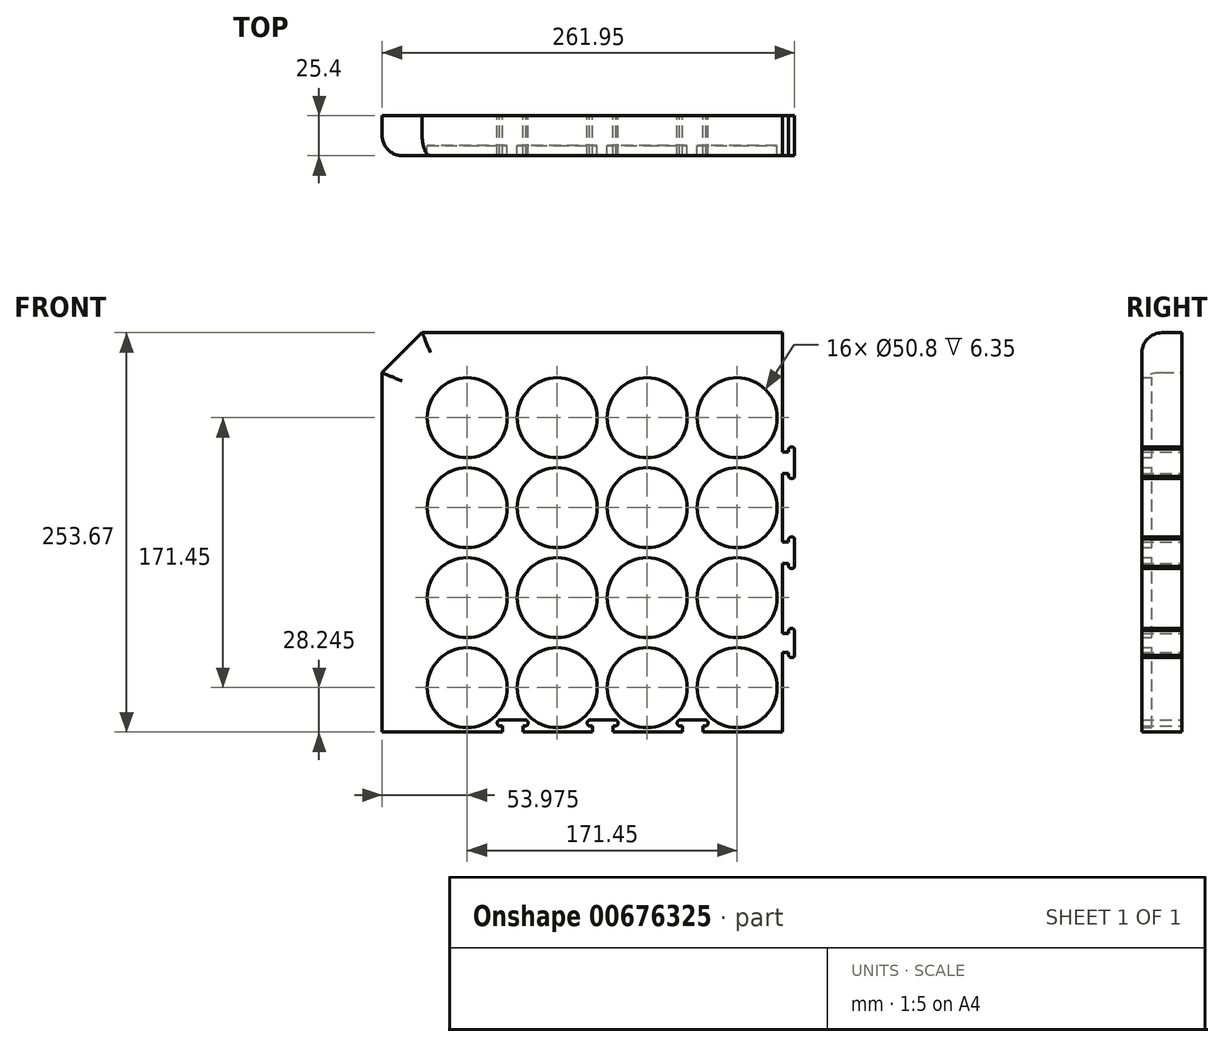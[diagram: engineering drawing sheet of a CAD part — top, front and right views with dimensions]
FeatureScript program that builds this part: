
annotation { "Feature Type Name" : "Feature", "Feature Type Description" : "" }
export const myFeature = defineFeature(function(context is Context, id is Id, definition is map)
    precondition{}
    {
        {
            var Q0;
            Q0=qCreatedBy(makeId("Front.planeOp"),FACE);
            var sketch = newSketch(context, id + "F0", { "sketchPlane" : qUnion([Q0])});
            skLineSegment(sketch, "E0", {"start": v(0, 0) * mm, "end": v(457.2, 0) * mm});
            skLineSegment(sketch, "E1", {"start": v(457.2, 0) * mm, "end": v(457.2, 457.2) * mm});
            skLineSegment(sketch, "E2", {"start": v(0, 0) * mm, "end": v(0, 457.2) * mm});
            skLineSegment(sketch, "E3", {"start": v(0, 457.2) * mm, "end": v(457.2, 457.2) * mm});
            skLineSegment(sketch, "E4", {"start": v(0, 457.2) * mm, "end": v(57.15, 457.2) * mm, "construction": true});
            skLineSegment(sketch, "E5", {"start": v(0, 457.2) * mm, "end": v(0, 400.05) * mm});
            skLineSegment(sketch, "E6", {"start": v(0, 400.05) * mm, "end": v(57.15, 400.05) * mm, "construction": true});
            skLineSegment(sketch, "E7", {"start": v(57.15, 457.2) * mm, "end": v(57.15, 400.05) * mm, "construction": true});
            skLineSegment(sketch, "E8", {"start": v(0, 457.2) * mm, "end": v(57.15, 400.05) * mm, "construction": true});
            skPoint(sketch, "E9.first.point", {"position": v(0, 428.63) * mm});
            skPoint(sketch, "E9.second.point", {"position": v(57.15, 428.63) * mm});
            skPoint(sketch, "E9.third.point", {"position": v(28.58, 457.2) * mm});
            skCircle(sketch, "E10", {"center": v(28.58, 428.63) * mm, "radius": 25.4 * mm});
            skCircle(sketch, "E11.0.1.0", {"center": v(28.58, 371.48) * mm, "radius": 25.4 * mm});
            skCircle(sketch, "E11.0.2.0", {"center": v(28.58, 314.32) * mm, "radius": 25.4 * mm});
            skCircle(sketch, "E11.0.3.0", {"center": v(28.58, 257.17) * mm, "radius": 25.4 * mm});
            skCircle(sketch, "E11.0.4.0", {"center": v(28.58, 200.02) * mm, "radius": 25.4 * mm});
            skCircle(sketch, "E11.0.5.0", {"center": v(28.58, 142.87) * mm, "radius": 25.4 * mm});
            skCircle(sketch, "E11.0.6.0", {"center": v(28.58, 85.72) * mm, "radius": 25.4 * mm});
            skCircle(sketch, "E11.0.7.0", {"center": v(28.58, 28.57) * mm, "radius": 25.4 * mm});
            skCircle(sketch, "E11.1.0.0", {"center": v(85.73, 428.63) * mm, "radius": 25.4 * mm});
            skCircle(sketch, "E11.1.1.0", {"center": v(85.73, 371.48) * mm, "radius": 25.4 * mm});
            skCircle(sketch, "E11.1.2.0", {"center": v(85.73, 314.32) * mm, "radius": 25.4 * mm});
            skCircle(sketch, "E11.1.3.0", {"center": v(85.73, 257.17) * mm, "radius": 25.4 * mm});
            skCircle(sketch, "E11.1.4.0", {"center": v(85.73, 200.02) * mm, "radius": 25.4 * mm});
            skCircle(sketch, "E11.1.5.0", {"center": v(85.73, 142.87) * mm, "radius": 25.4 * mm});
            skCircle(sketch, "E11.1.6.0", {"center": v(85.73, 85.72) * mm, "radius": 25.4 * mm});
            skCircle(sketch, "E11.1.7.0", {"center": v(85.73, 28.57) * mm, "radius": 25.4 * mm});
            skCircle(sketch, "E11.2.0.0", {"center": v(142.88, 428.63) * mm, "radius": 25.4 * mm});
            skCircle(sketch, "E11.2.1.0", {"center": v(142.88, 371.48) * mm, "radius": 25.4 * mm});
            skCircle(sketch, "E11.2.2.0", {"center": v(142.88, 314.32) * mm, "radius": 25.4 * mm});
            skCircle(sketch, "E11.2.3.0", {"center": v(142.88, 257.17) * mm, "radius": 25.4 * mm});
            skCircle(sketch, "E11.2.4.0", {"center": v(142.88, 200.02) * mm, "radius": 25.4 * mm});
            skCircle(sketch, "E11.2.5.0", {"center": v(142.88, 142.87) * mm, "radius": 25.4 * mm});
            skCircle(sketch, "E11.2.6.0", {"center": v(142.88, 85.72) * mm, "radius": 25.4 * mm});
            skCircle(sketch, "E11.2.7.0", {"center": v(142.88, 28.57) * mm, "radius": 25.4 * mm});
            skCircle(sketch, "E11.3.0.0", {"center": v(200.03, 428.63) * mm, "radius": 25.4 * mm});
            skCircle(sketch, "E11.3.1.0", {"center": v(200.03, 371.48) * mm, "radius": 25.4 * mm});
            skCircle(sketch, "E11.3.2.0", {"center": v(200.03, 314.32) * mm, "radius": 25.4 * mm});
            skCircle(sketch, "E11.3.3.0", {"center": v(200.03, 257.17) * mm, "radius": 25.4 * mm});
            skCircle(sketch, "E11.3.4.0", {"center": v(200.03, 200.02) * mm, "radius": 25.4 * mm});
            skCircle(sketch, "E11.3.5.0", {"center": v(200.03, 142.87) * mm, "radius": 25.4 * mm});
            skCircle(sketch, "E11.3.6.0", {"center": v(200.03, 85.72) * mm, "radius": 25.4 * mm});
            skCircle(sketch, "E11.3.7.0", {"center": v(200.03, 28.57) * mm, "radius": 25.4 * mm});
            skCircle(sketch, "E11.4.0.0", {"center": v(257.18, 428.63) * mm, "radius": 25.4 * mm});
            skCircle(sketch, "E11.4.1.0", {"center": v(257.18, 371.48) * mm, "radius": 25.4 * mm});
            skCircle(sketch, "E11.4.2.0", {"center": v(257.18, 314.32) * mm, "radius": 25.4 * mm});
            skCircle(sketch, "E11.4.3.0", {"center": v(257.18, 257.17) * mm, "radius": 25.4 * mm});
            skCircle(sketch, "E11.4.4.0", {"center": v(257.18, 200.02) * mm, "radius": 25.4 * mm});
            skCircle(sketch, "E11.4.5.0", {"center": v(257.18, 142.87) * mm, "radius": 25.4 * mm});
            skCircle(sketch, "E11.4.6.0", {"center": v(257.18, 85.72) * mm, "radius": 25.4 * mm});
            skCircle(sketch, "E11.4.7.0", {"center": v(257.18, 28.57) * mm, "radius": 25.4 * mm});
            skCircle(sketch, "E11.5.0.0", {"center": v(314.33, 428.63) * mm, "radius": 25.4 * mm});
            skCircle(sketch, "E11.5.1.0", {"center": v(314.33, 371.48) * mm, "radius": 25.4 * mm});
            skCircle(sketch, "E11.5.2.0", {"center": v(314.33, 314.32) * mm, "radius": 25.4 * mm});
            skCircle(sketch, "E11.5.3.0", {"center": v(314.33, 257.17) * mm, "radius": 25.4 * mm});
            skCircle(sketch, "E11.5.4.0", {"center": v(314.33, 200.02) * mm, "radius": 25.4 * mm});
            skCircle(sketch, "E11.5.5.0", {"center": v(314.33, 142.87) * mm, "radius": 25.4 * mm});
            skCircle(sketch, "E11.5.6.0", {"center": v(314.33, 85.72) * mm, "radius": 25.4 * mm});
            skCircle(sketch, "E11.5.7.0", {"center": v(314.33, 28.57) * mm, "radius": 25.4 * mm});
            skCircle(sketch, "E11.6.0.0", {"center": v(371.48, 428.63) * mm, "radius": 25.4 * mm});
            skCircle(sketch, "E11.6.1.0", {"center": v(371.48, 371.48) * mm, "radius": 25.4 * mm});
            skCircle(sketch, "E11.6.2.0", {"center": v(371.48, 314.32) * mm, "radius": 25.4 * mm});
            skCircle(sketch, "E11.6.3.0", {"center": v(371.48, 257.17) * mm, "radius": 25.4 * mm});
            skCircle(sketch, "E11.6.4.0", {"center": v(371.48, 200.02) * mm, "radius": 25.4 * mm});
            skCircle(sketch, "E11.6.5.0", {"center": v(371.48, 142.87) * mm, "radius": 25.4 * mm});
            skCircle(sketch, "E11.6.6.0", {"center": v(371.48, 85.72) * mm, "radius": 25.4 * mm});
            skCircle(sketch, "E11.6.7.0", {"center": v(371.48, 28.57) * mm, "radius": 25.4 * mm});
            skCircle(sketch, "E11.7.0.0", {"center": v(428.63, 428.63) * mm, "radius": 25.4 * mm});
            skCircle(sketch, "E11.7.1.0", {"center": v(428.63, 371.48) * mm, "radius": 25.4 * mm});
            skCircle(sketch, "E11.7.2.0", {"center": v(428.63, 314.32) * mm, "radius": 25.4 * mm});
            skCircle(sketch, "E11.7.3.0", {"center": v(428.63, 257.17) * mm, "radius": 25.4 * mm});
            skCircle(sketch, "E11.7.4.0", {"center": v(428.63, 200.02) * mm, "radius": 25.4 * mm});
            skCircle(sketch, "E11.7.5.0", {"center": v(428.63, 142.87) * mm, "radius": 25.4 * mm});
            skCircle(sketch, "E11.7.6.0", {"center": v(428.63, 85.72) * mm, "radius": 25.4 * mm});
            skCircle(sketch, "E11.7.7.0", {"center": v(428.63, 28.57) * mm, "radius": 25.4 * mm});
            skLineSegment(sketch, "E11.direction1", {"start": v(28.58, 428.63) * mm, "end": v(85.73, 428.63) * mm, "construction": true});
            skLineSegment(sketch, "E11.direction2", {"start": v(28.58, 428.63) * mm, "end": v(28.58, 371.48) * mm, "construction": true});
            skLineSegment(sketch, "E12", {"start": v(0, 457.2) * mm, "end": v(0, 228.6) * mm, "construction": true});
            skLineSegment(sketch, "E13", {"start": v(0, 228.6) * mm, "end": v(-25.4, 228.6) * mm, "construction": true});
            skLineSegment(sketch, "E14", {"start": v(0, 0) * mm, "end": v(-25.4, 0) * mm, "construction": true});
            skLineSegment(sketch, "E15", {"start": v(0, 0) * mm, "end": v(0, -25.4) * mm, "construction": true});
            skLineSegment(sketch, "E16", {"start": v(457.2, 0) * mm, "end": v(458.14, -25.38) * mm, "construction": true});
            skLineSegment(sketch, "E17", {"start": v(457.2, 0) * mm, "end": v(482.58, 0.94) * mm, "construction": true});
            skLineSegment(sketch, "E18", {"start": v(457.2, 457.2) * mm, "end": v(457.2, 482.6) * mm, "construction": true});
            skLineSegment(sketch, "E19", {"start": v(457.2, 457.2) * mm, "end": v(482.6, 457.2) * mm, "construction": true});
            skLineSegment(sketch, "E20", {"start": v(0, 457.2) * mm, "end": v(0, 482.6) * mm, "construction": true});
            skLineSegment(sketch, "E21", {"start": v(0, 457.2) * mm, "end": v(-25.4, 457.2) * mm, "construction": true});
            skLineSegment(sketch, "E22", {"start": v(-25.4, 228.6) * mm, "end": v(-25.4, 0) * mm});
            skLineSegment(sketch, "E23", {"start": v(0, -25.4) * mm, "end": v(-25.4, 0) * mm});
            skLineSegment(sketch, "E24", {"start": v(0, -25.4) * mm, "end": v(458.14, -25.38) * mm});
            skLineSegment(sketch, "E25", {"start": v(458.14, -25.38) * mm, "end": v(482.58, 0.94) * mm});
            skLineSegment(sketch, "E26", {"start": v(482.58, 0.94) * mm, "end": v(482.6, 457.2) * mm});
            skLineSegment(sketch, "E27", {"start": v(482.6, 457.2) * mm, "end": v(457.2, 482.6) * mm});
            skLineSegment(sketch, "E28", {"start": v(457.2, 482.6) * mm, "end": v(0, 482.6) * mm});
            skLineSegment(sketch, "E29", {"start": v(0, 482.6) * mm, "end": v(-25.4, 457.2) * mm});
            skLineSegment(sketch, "E30", {"start": v(-25.4, 457.2) * mm, "end": v(-25.4, 228.6) * mm});
            skLineSegment(sketch, "E31", {"start": v(229.07, -25.4) * mm, "end": v(229.07, 482.6) * mm, "construction": true});
            skLineSegment(sketch, "E32", {"start": v(482.6, 228.6) * mm, "end": v(-25.4, 228.6) * mm, "construction": true});
            skPoint(sketch, "E32.startSnap0", {"position": v(457.2, 228.6) * mm});
            skSolve(sketch);
        }
        {
            var Q0;
            Q0=makeQuery(id+"F0.imprint","IMPRINT",FACE,{"disambiguationData":[TD([[makeQuery(id+"F0.imprint","IMPRINT",EDGE,{"derivedFrom":sQuery(id+"F0.wireOp",EDGE,"E0")}),1.0]])]});
            var Q1;
            Q1=makeQuery(id+"F0.imprint","IMPRINT",FACE,{"disambiguationData":[TD([[makeQuery(id+"F0.imprint","IMPRINT",EDGE,{"derivedFrom":sQuery(id+"F0.wireOp",EDGE,"E0")}),-1.0]])]});
            extrude(context, id + "F1", {"entities" : qUnion([Q0, Q1]), "depth" : 25.4 * mm, "offsetDistance" : 25.4 * mm});
        }
        {
            var Q0;
            Q0=makeQuery(id+"F0.imprint","IMPRINT",FACE,{"disambiguationData":[TD([[makeQuery(id+"F0.imprint","IMPRINT",EDGE,{"derivedFrom":sQuery(id+"F0.wireOp",EDGE,"E10")}),1.0]])]});
            var Q1;
            Q1=makeQuery(id+"F0.imprint","IMPRINT",FACE,{"disambiguationData":[TD([[makeQuery(id+"F0.imprint","IMPRINT",EDGE,{"derivedFrom":sQuery(id+"F0.wireOp",EDGE,"E11.1.0.0")}),1.0]])]});
            var Q2;
            Q2=makeQuery(id+"F0.imprint","IMPRINT",FACE,{"disambiguationData":[TD([[makeQuery(id+"F0.imprint","IMPRINT",EDGE,{"derivedFrom":sQuery(id+"F0.wireOp",EDGE,"E11.2.0.0")}),1.0]])]});
            var Q3;
            Q3=makeQuery(id+"F0.imprint","IMPRINT",FACE,{"disambiguationData":[TD([[makeQuery(id+"F0.imprint","IMPRINT",EDGE,{"derivedFrom":sQuery(id+"F0.wireOp",EDGE,"E11.3.0.0")}),1.0]])]});
            var Q4;
            Q4=makeQuery(id+"F0.imprint","IMPRINT",FACE,{"disambiguationData":[TD([[makeQuery(id+"F0.imprint","IMPRINT",EDGE,{"derivedFrom":sQuery(id+"F0.wireOp",EDGE,"E11.4.0.0")}),1.0]])]});
            var Q5;
            Q5=makeQuery(id+"F0.imprint","IMPRINT",FACE,{"disambiguationData":[TD([[makeQuery(id+"F0.imprint","IMPRINT",EDGE,{"derivedFrom":sQuery(id+"F0.wireOp",EDGE,"E11.5.0.0")}),1.0]])]});
            var Q6;
            Q6=makeQuery(id+"F0.imprint","IMPRINT",FACE,{"disambiguationData":[TD([[makeQuery(id+"F0.imprint","IMPRINT",EDGE,{"derivedFrom":sQuery(id+"F0.wireOp",EDGE,"E11.6.0.0")}),1.0]])]});
            var Q7;
            Q7=makeQuery(id+"F0.imprint","IMPRINT",FACE,{"disambiguationData":[TD([[makeQuery(id+"F0.imprint","IMPRINT",EDGE,{"derivedFrom":sQuery(id+"F0.wireOp",EDGE,"E11.7.0.0")}),1.0]])]});
            var Q8;
            Q8=makeQuery(id+"F0.imprint","IMPRINT",FACE,{"disambiguationData":[TD([[makeQuery(id+"F0.imprint","IMPRINT",EDGE,{"derivedFrom":sQuery(id+"F0.wireOp",EDGE,"E11.7.1.0")}),1.0]])]});
            var Q9;
            Q9=makeQuery(id+"F0.imprint","IMPRINT",FACE,{"disambiguationData":[TD([[makeQuery(id+"F0.imprint","IMPRINT",EDGE,{"derivedFrom":sQuery(id+"F0.wireOp",EDGE,"E11.6.1.0")}),1.0]])]});
            var Q10;
            Q10=makeQuery(id+"F0.imprint","IMPRINT",FACE,{"disambiguationData":[TD([[makeQuery(id+"F0.imprint","IMPRINT",EDGE,{"derivedFrom":sQuery(id+"F0.wireOp",EDGE,"E11.5.1.0")}),1.0]])]});
            var Q11;
            Q11=makeQuery(id+"F0.imprint","IMPRINT",FACE,{"disambiguationData":[TD([[makeQuery(id+"F0.imprint","IMPRINT",EDGE,{"derivedFrom":sQuery(id+"F0.wireOp",EDGE,"E11.4.1.0")}),1.0]])]});
            var Q12;
            Q12=makeQuery(id+"F0.imprint","IMPRINT",FACE,{"disambiguationData":[TD([[makeQuery(id+"F0.imprint","IMPRINT",EDGE,{"derivedFrom":sQuery(id+"F0.wireOp",EDGE,"E11.3.1.0")}),1.0]])]});
            var Q13;
            Q13=makeQuery(id+"F0.imprint","IMPRINT",FACE,{"disambiguationData":[TD([[makeQuery(id+"F0.imprint","IMPRINT",EDGE,{"derivedFrom":sQuery(id+"F0.wireOp",EDGE,"E11.2.3.0")}),1.0]])]});
            var Q14;
            Q14=makeQuery(id+"F0.imprint","IMPRINT",FACE,{"disambiguationData":[TD([[makeQuery(id+"F0.imprint","IMPRINT",EDGE,{"derivedFrom":sQuery(id+"F0.wireOp",EDGE,"E11.6.3.0")}),1.0]])]});
            var Q15;
            Q15=makeQuery(id+"F0.imprint","IMPRINT",FACE,{"disambiguationData":[TD([[makeQuery(id+"F0.imprint","IMPRINT",EDGE,{"derivedFrom":sQuery(id+"F0.wireOp",EDGE,"E11.4.3.0")}),1.0]])]});
            var Q16;
            Q16=makeQuery(id+"F0.imprint","IMPRINT",FACE,{"disambiguationData":[TD([[makeQuery(id+"F0.imprint","IMPRINT",EDGE,{"derivedFrom":sQuery(id+"F0.wireOp",EDGE,"E11.5.2.0")}),1.0]])]});
            var Q17;
            Q17=makeQuery(id+"F0.imprint","IMPRINT",FACE,{"disambiguationData":[TD([[makeQuery(id+"F0.imprint","IMPRINT",EDGE,{"derivedFrom":sQuery(id+"F0.wireOp",EDGE,"E11.3.2.0")}),1.0]])]});
            var Q18;
            Q18=makeQuery(id+"F0.imprint","IMPRINT",FACE,{"disambiguationData":[TD([[makeQuery(id+"F0.imprint","IMPRINT",EDGE,{"derivedFrom":sQuery(id+"F0.wireOp",EDGE,"E11.2.4.0")}),1.0]])]});
            var Q19;
            Q19=makeQuery(id+"F0.imprint","IMPRINT",FACE,{"disambiguationData":[TD([[makeQuery(id+"F0.imprint","IMPRINT",EDGE,{"derivedFrom":sQuery(id+"F0.wireOp",EDGE,"E11.6.4.0")}),1.0]])]});
            var Q20;
            Q20=makeQuery(id+"F0.imprint","IMPRINT",FACE,{"disambiguationData":[TD([[makeQuery(id+"F0.imprint","IMPRINT",EDGE,{"derivedFrom":sQuery(id+"F0.wireOp",EDGE,"E11.5.5.0")}),1.0]])]});
            var Q21;
            Q21=makeQuery(id+"F0.imprint","IMPRINT",FACE,{"disambiguationData":[TD([[makeQuery(id+"F0.imprint","IMPRINT",EDGE,{"derivedFrom":sQuery(id+"F0.wireOp",EDGE,"E11.3.5.0")}),1.0]])]});
            var Q22;
            Q22=makeQuery(id+"F0.imprint","IMPRINT",FACE,{"disambiguationData":[TD([[makeQuery(id+"F0.imprint","IMPRINT",EDGE,{"derivedFrom":sQuery(id+"F0.wireOp",EDGE,"E11.4.4.0")}),1.0]])]});
            var Q23;
            Q23=makeQuery(id+"F0.imprint","IMPRINT",FACE,{"disambiguationData":[TD([[makeQuery(id+"F0.imprint","IMPRINT",EDGE,{"derivedFrom":sQuery(id+"F0.wireOp",EDGE,"E11.5.3.0")}),1.0]])]});
            var Q24;
            Q24=makeQuery(id+"F0.imprint","IMPRINT",FACE,{"disambiguationData":[TD([[makeQuery(id+"F0.imprint","IMPRINT",EDGE,{"derivedFrom":sQuery(id+"F0.wireOp",EDGE,"E11.3.3.0")}),1.0]])]});
            var Q25;
            Q25=makeQuery(id+"F0.imprint","IMPRINT",FACE,{"disambiguationData":[TD([[makeQuery(id+"F0.imprint","IMPRINT",EDGE,{"derivedFrom":sQuery(id+"F0.wireOp",EDGE,"E11.2.5.0")}),1.0]])]});
            var Q26;
            Q26=makeQuery(id+"F0.imprint","IMPRINT",FACE,{"disambiguationData":[TD([[makeQuery(id+"F0.imprint","IMPRINT",EDGE,{"derivedFrom":sQuery(id+"F0.wireOp",EDGE,"E11.6.5.0")}),1.0]])]});
            var Q27;
            Q27=makeQuery(id+"F0.imprint","IMPRINT",FACE,{"disambiguationData":[TD([[makeQuery(id+"F0.imprint","IMPRINT",EDGE,{"derivedFrom":sQuery(id+"F0.wireOp",EDGE,"E11.5.6.0")}),1.0]])]});
            var Q28;
            Q28=makeQuery(id+"F0.imprint","IMPRINT",FACE,{"disambiguationData":[TD([[makeQuery(id+"F0.imprint","IMPRINT",EDGE,{"derivedFrom":sQuery(id+"F0.wireOp",EDGE,"E11.4.5.0")}),1.0]])]});
            var Q29;
            Q29=makeQuery(id+"F0.imprint","IMPRINT",FACE,{"disambiguationData":[TD([[makeQuery(id+"F0.imprint","IMPRINT",EDGE,{"derivedFrom":sQuery(id+"F0.wireOp",EDGE,"E11.3.6.0")}),1.0]])]});
            var Q30;
            Q30=makeQuery(id+"F0.imprint","IMPRINT",FACE,{"disambiguationData":[TD([[makeQuery(id+"F0.imprint","IMPRINT",EDGE,{"derivedFrom":sQuery(id+"F0.wireOp",EDGE,"E11.5.4.0")}),1.0]])]});
            var Q31;
            Q31=makeQuery(id+"F0.imprint","IMPRINT",FACE,{"disambiguationData":[TD([[makeQuery(id+"F0.imprint","IMPRINT",EDGE,{"derivedFrom":sQuery(id+"F0.wireOp",EDGE,"E11.3.4.0")}),1.0]])]});
            var Q32;
            Q32=makeQuery(id+"F0.imprint","IMPRINT",FACE,{"disambiguationData":[TD([[makeQuery(id+"F0.imprint","IMPRINT",EDGE,{"derivedFrom":sQuery(id+"F0.wireOp",EDGE,"E11.6.6.0")}),1.0]])]});
            var Q33;
            Q33=makeQuery(id+"F0.imprint","IMPRINT",FACE,{"disambiguationData":[TD([[makeQuery(id+"F0.imprint","IMPRINT",EDGE,{"derivedFrom":sQuery(id+"F0.wireOp",EDGE,"E11.4.6.0")}),1.0]])]});
            var Q34;
            Q34=makeQuery(id+"F0.imprint","IMPRINT",FACE,{"disambiguationData":[TD([[makeQuery(id+"F0.imprint","IMPRINT",EDGE,{"derivedFrom":sQuery(id+"F0.wireOp",EDGE,"E11.2.6.0")}),1.0]])]});
            var Q35;
            Q35=makeQuery(id+"F0.imprint","IMPRINT",FACE,{"disambiguationData":[TD([[makeQuery(id+"F0.imprint","IMPRINT",EDGE,{"derivedFrom":sQuery(id+"F0.wireOp",EDGE,"E11.1.5.0")}),1.0]])]});
            var Q36;
            Q36=makeQuery(id+"F0.imprint","IMPRINT",FACE,{"disambiguationData":[TD([[makeQuery(id+"F0.imprint","IMPRINT",EDGE,{"derivedFrom":sQuery(id+"F0.wireOp",EDGE,"E11.1.6.0")}),1.0]])]});
            var Q37;
            Q37=makeQuery(id+"F0.imprint","IMPRINT",FACE,{"disambiguationData":[TD([[makeQuery(id+"F0.imprint","IMPRINT",EDGE,{"derivedFrom":sQuery(id+"F0.wireOp",EDGE,"E11.1.1.0")}),1.0]])]});
            var Q38;
            Q38=makeQuery(id+"F0.imprint","IMPRINT",FACE,{"disambiguationData":[TD([[makeQuery(id+"F0.imprint","IMPRINT",EDGE,{"derivedFrom":sQuery(id+"F0.wireOp",EDGE,"E11.1.2.0")}),1.0]])]});
            var Q39;
            Q39=makeQuery(id+"F0.imprint","IMPRINT",FACE,{"disambiguationData":[TD([[makeQuery(id+"F0.imprint","IMPRINT",EDGE,{"derivedFrom":sQuery(id+"F0.wireOp",EDGE,"E11.1.3.0")}),1.0]])]});
            var Q40;
            Q40=makeQuery(id+"F0.imprint","IMPRINT",FACE,{"disambiguationData":[TD([[makeQuery(id+"F0.imprint","IMPRINT",EDGE,{"derivedFrom":sQuery(id+"F0.wireOp",EDGE,"E11.1.4.0")}),1.0]])]});
            var Q41;
            Q41=makeQuery(id+"F0.imprint","IMPRINT",FACE,{"disambiguationData":[TD([[makeQuery(id+"F0.imprint","IMPRINT",EDGE,{"derivedFrom":sQuery(id+"F0.wireOp",EDGE,"E11.2.1.0")}),1.0]])]});
            var Q42;
            Q42=makeQuery(id+"F0.imprint","IMPRINT",FACE,{"disambiguationData":[TD([[makeQuery(id+"F0.imprint","IMPRINT",EDGE,{"derivedFrom":sQuery(id+"F0.wireOp",EDGE,"E11.2.2.0")}),1.0]])]});
            var Q43;
            Q43=makeQuery(id+"F0.imprint","IMPRINT",FACE,{"disambiguationData":[TD([[makeQuery(id+"F0.imprint","IMPRINT",EDGE,{"derivedFrom":sQuery(id+"F0.wireOp",EDGE,"E11.6.2.0")}),1.0]])]});
            var Q44;
            Q44=makeQuery(id+"F0.imprint","IMPRINT",FACE,{"disambiguationData":[TD([[makeQuery(id+"F0.imprint","IMPRINT",EDGE,{"derivedFrom":sQuery(id+"F0.wireOp",EDGE,"E11.4.2.0")}),1.0]])]});
            var Q45;
            Q45=makeQuery(id+"F0.imprint","IMPRINT",FACE,{"disambiguationData":[TD([[makeQuery(id+"F0.imprint","IMPRINT",EDGE,{"derivedFrom":sQuery(id+"F0.wireOp",EDGE,"E11.7.7.0")}),1.0]])]});
            var Q46;
            Q46=makeQuery(id+"F0.imprint","IMPRINT",FACE,{"disambiguationData":[TD([[makeQuery(id+"F0.imprint","IMPRINT",EDGE,{"derivedFrom":sQuery(id+"F0.wireOp",EDGE,"E11.7.6.0")}),1.0]])]});
            var Q47;
            Q47=makeQuery(id+"F0.imprint","IMPRINT",FACE,{"disambiguationData":[TD([[makeQuery(id+"F0.imprint","IMPRINT",EDGE,{"derivedFrom":sQuery(id+"F0.wireOp",EDGE,"E11.7.5.0")}),1.0]])]});
            var Q48;
            Q48=makeQuery(id+"F0.imprint","IMPRINT",FACE,{"disambiguationData":[TD([[makeQuery(id+"F0.imprint","IMPRINT",EDGE,{"derivedFrom":sQuery(id+"F0.wireOp",EDGE,"E11.7.4.0")}),1.0]])]});
            var Q49;
            Q49=makeQuery(id+"F0.imprint","IMPRINT",FACE,{"disambiguationData":[TD([[makeQuery(id+"F0.imprint","IMPRINT",EDGE,{"derivedFrom":sQuery(id+"F0.wireOp",EDGE,"E11.7.3.0")}),1.0]])]});
            var Q50;
            Q50=makeQuery(id+"F0.imprint","IMPRINT",FACE,{"disambiguationData":[TD([[makeQuery(id+"F0.imprint","IMPRINT",EDGE,{"derivedFrom":sQuery(id+"F0.wireOp",EDGE,"E11.7.2.0")}),1.0]])]});
            var Q51;
            Q51=makeQuery(id+"F0.imprint","IMPRINT",FACE,{"disambiguationData":[TD([[makeQuery(id+"F0.imprint","IMPRINT",EDGE,{"derivedFrom":sQuery(id+"F0.wireOp",EDGE,"E11.6.7.0")}),1.0]])]});
            var Q52;
            Q52=makeQuery(id+"F0.imprint","IMPRINT",FACE,{"disambiguationData":[TD([[makeQuery(id+"F0.imprint","IMPRINT",EDGE,{"derivedFrom":sQuery(id+"F0.wireOp",EDGE,"E11.5.7.0")}),1.0]])]});
            var Q53;
            Q53=makeQuery(id+"F0.imprint","IMPRINT",FACE,{"disambiguationData":[TD([[makeQuery(id+"F0.imprint","IMPRINT",EDGE,{"derivedFrom":sQuery(id+"F0.wireOp",EDGE,"E11.4.7.0")}),1.0]])]});
            var Q54;
            Q54=makeQuery(id+"F0.imprint","IMPRINT",FACE,{"disambiguationData":[TD([[makeQuery(id+"F0.imprint","IMPRINT",EDGE,{"derivedFrom":sQuery(id+"F0.wireOp",EDGE,"E11.3.7.0")}),1.0]])]});
            var Q55;
            Q55=makeQuery(id+"F0.imprint","IMPRINT",FACE,{"disambiguationData":[TD([[makeQuery(id+"F0.imprint","IMPRINT",EDGE,{"derivedFrom":sQuery(id+"F0.wireOp",EDGE,"E11.2.7.0")}),1.0]])]});
            var Q56;
            Q56=makeQuery(id+"F0.imprint","IMPRINT",FACE,{"disambiguationData":[TD([[makeQuery(id+"F0.imprint","IMPRINT",EDGE,{"derivedFrom":sQuery(id+"F0.wireOp",EDGE,"E11.1.7.0")}),1.0]])]});
            var Q57;
            Q57=makeQuery(id+"F0.imprint","IMPRINT",FACE,{"disambiguationData":[TD([[makeQuery(id+"F0.imprint","IMPRINT",EDGE,{"derivedFrom":sQuery(id+"F0.wireOp",EDGE,"E11.0.7.0")}),1.0]])]});
            var Q58;
            Q58=makeQuery(id+"F0.imprint","IMPRINT",FACE,{"disambiguationData":[TD([[makeQuery(id+"F0.imprint","IMPRINT",EDGE,{"derivedFrom":sQuery(id+"F0.wireOp",EDGE,"E11.0.6.0")}),1.0]])]});
            var Q59;
            Q59=makeQuery(id+"F0.imprint","IMPRINT",FACE,{"disambiguationData":[TD([[makeQuery(id+"F0.imprint","IMPRINT",EDGE,{"derivedFrom":sQuery(id+"F0.wireOp",EDGE,"E11.0.5.0")}),1.0]])]});
            var Q60;
            Q60=makeQuery(id+"F0.imprint","IMPRINT",FACE,{"disambiguationData":[TD([[makeQuery(id+"F0.imprint","IMPRINT",EDGE,{"derivedFrom":sQuery(id+"F0.wireOp",EDGE,"E11.0.4.0")}),1.0]])]});
            var Q61;
            Q61=makeQuery(id+"F0.imprint","IMPRINT",FACE,{"disambiguationData":[TD([[makeQuery(id+"F0.imprint","IMPRINT",EDGE,{"derivedFrom":sQuery(id+"F0.wireOp",EDGE,"E11.0.3.0")}),1.0]])]});
            var Q62;
            Q62=makeQuery(id+"F0.imprint","IMPRINT",FACE,{"disambiguationData":[TD([[makeQuery(id+"F0.imprint","IMPRINT",EDGE,{"derivedFrom":sQuery(id+"F0.wireOp",EDGE,"E11.0.2.0")}),1.0]])]});
            var Q63;
            Q63=makeQuery(id+"F0.imprint","IMPRINT",FACE,{"disambiguationData":[TD([[makeQuery(id+"F0.imprint","IMPRINT",EDGE,{"derivedFrom":sQuery(id+"F0.wireOp",EDGE,"E11.0.1.0")}),1.0]])]});
            extrude(context, id + "F2", {"entities" : qUnion([Q0, Q1, Q2, Q3, Q4, Q5, Q6, Q7, Q8, Q9, Q10, Q11, Q12, Q13, Q14, Q15, Q16, Q17, Q18, Q19, Q20, Q21, Q22, Q23, Q24, Q25, Q26, Q27, Q28, Q29, Q30, Q31, Q32, Q33, Q34, Q35, Q36, Q37, Q38, Q39, Q40, Q41, Q42, Q43, Q44, Q45, Q46, Q47, Q48, Q49, Q50, Q51, Q52, Q53, Q54, Q55, Q56, Q57, Q58, Q59, Q60, Q61, Q62, Q63]), "operationType" : NewBodyOperationType.ADD, "depth" : 19.05 * mm, "offsetDistance" : 25.4 * mm});
        }
        {
            var Q0;
            Q0=makeQuery(id+"F1.opExtrude","CAP_EDGE",EDGE,{"disambiguationData":[OSD([sQuery(id+"F0.wireOp",EDGE,"E22"),sQuery(id+"F0.wireOp",EDGE,"E30")])],"isStart":false});
            var Q1;
            Q1=makeQuery(id+"F1.opExtrude","CAP_EDGE",EDGE,{"disambiguationData":[OSD([sQuery(id+"F0.wireOp",EDGE,"E29")])],"isStart":false});
            var Q2;
            Q2=makeQuery(id+"F1.opExtrude","CAP_EDGE",EDGE,{"disambiguationData":[OSD([sQuery(id+"F0.wireOp",EDGE,"E28")])],"isStart":false});
            var Q3;
            Q3=makeQuery(id+"F1.opExtrude","CAP_EDGE",EDGE,{"disambiguationData":[OSD([sQuery(id+"F0.wireOp",EDGE,"E27")])],"isStart":false});
            var Q4;
            Q4=makeQuery(id+"F1.opExtrude","CAP_EDGE",EDGE,{"disambiguationData":[OSD([sQuery(id+"F0.wireOp",EDGE,"E26")])],"isStart":false});
            var Q5;
            Q5=makeQuery(id+"F1.opExtrude","CAP_EDGE",EDGE,{"disambiguationData":[OSD([sQuery(id+"F0.wireOp",EDGE,"E23")])],"isStart":false});
            var Q6;
            Q6=makeQuery(id+"F1.opExtrude","CAP_EDGE",EDGE,{"disambiguationData":[OSD([sQuery(id+"F0.wireOp",EDGE,"E24")])],"isStart":false});
            var Q7;
            Q7=makeQuery(id+"F1.opExtrude","CAP_EDGE",EDGE,{"disambiguationData":[OSD([sQuery(id+"F0.wireOp",EDGE,"E25")])],"isStart":false});
            fillet(context, id + "F3", {"entities" : qUnion([Q0, Q1, Q2, Q3, Q4, Q5, Q6, Q7]), "radius" : 12.7 * mm, "tangentPropagation" : true, "allowEdgeOverflow" : false});
        }
        {
            var Q0;
            Q0=makeQuery(id+"F1.opExtrude","CAP_FACE",FACE,{"disambiguationData":[OSD([sQuery(id+"F0.wireOp",EDGE,"E10"),sQuery(id+"F0.wireOp",EDGE,"E11.0.1.0"),sQuery(id+"F0.wireOp",EDGE,"E11.0.2.0"),sQuery(id+"F0.wireOp",EDGE,"E11.0.3.0"),sQuery(id+"F0.wireOp",EDGE,"E11.0.4.0"),sQuery(id+"F0.wireOp",EDGE,"E11.0.5.0"),sQuery(id+"F0.wireOp",EDGE,"E11.0.6.0"),sQuery(id+"F0.wireOp",EDGE,"E11.0.7.0"),sQuery(id+"F0.wireOp",EDGE,"E11.1.0.0"),sQuery(id+"F0.wireOp",EDGE,"E11.1.1.0"),sQuery(id+"F0.wireOp",EDGE,"E11.1.2.0"),sQuery(id+"F0.wireOp",EDGE,"E11.1.3.0"),sQuery(id+"F0.wireOp",EDGE,"E11.1.4.0"),sQuery(id+"F0.wireOp",EDGE,"E11.1.5.0"),sQuery(id+"F0.wireOp",EDGE,"E11.1.6.0"),sQuery(id+"F0.wireOp",EDGE,"E11.1.7.0"),sQuery(id+"F0.wireOp",EDGE,"E11.2.0.0"),sQuery(id+"F0.wireOp",EDGE,"E11.2.1.0"),sQuery(id+"F0.wireOp",EDGE,"E11.2.2.0"),sQuery(id+"F0.wireOp",EDGE,"E11.2.3.0"),sQuery(id+"F0.wireOp",EDGE,"E11.2.4.0"),sQuery(id+"F0.wireOp",EDGE,"E11.2.5.0"),sQuery(id+"F0.wireOp",EDGE,"E11.2.6.0"),sQuery(id+"F0.wireOp",EDGE,"E11.2.7.0"),sQuery(id+"F0.wireOp",EDGE,"E11.3.0.0"),sQuery(id+"F0.wireOp",EDGE,"E11.3.1.0"),sQuery(id+"F0.wireOp",EDGE,"E11.3.2.0"),sQuery(id+"F0.wireOp",EDGE,"E11.3.3.0"),sQuery(id+"F0.wireOp",EDGE,"E11.3.4.0"),sQuery(id+"F0.wireOp",EDGE,"E11.3.5.0"),sQuery(id+"F0.wireOp",EDGE,"E11.3.6.0"),sQuery(id+"F0.wireOp",EDGE,"E11.3.7.0"),sQuery(id+"F0.wireOp",EDGE,"E11.4.0.0"),sQuery(id+"F0.wireOp",EDGE,"E11.4.1.0"),sQuery(id+"F0.wireOp",EDGE,"E11.4.2.0"),sQuery(id+"F0.wireOp",EDGE,"E11.4.3.0"),sQuery(id+"F0.wireOp",EDGE,"E11.4.4.0"),sQuery(id+"F0.wireOp",EDGE,"E11.4.5.0"),sQuery(id+"F0.wireOp",EDGE,"E11.4.6.0"),sQuery(id+"F0.wireOp",EDGE,"E11.4.7.0"),sQuery(id+"F0.wireOp",EDGE,"E11.5.0.0"),sQuery(id+"F0.wireOp",EDGE,"E11.5.1.0"),sQuery(id+"F0.wireOp",EDGE,"E11.5.2.0"),sQuery(id+"F0.wireOp",EDGE,"E11.5.3.0"),sQuery(id+"F0.wireOp",EDGE,"E11.5.4.0"),sQuery(id+"F0.wireOp",EDGE,"E11.5.5.0"),sQuery(id+"F0.wireOp",EDGE,"E11.5.6.0"),sQuery(id+"F0.wireOp",EDGE,"E11.5.7.0"),sQuery(id+"F0.wireOp",EDGE,"E11.6.0.0"),sQuery(id+"F0.wireOp",EDGE,"E11.6.1.0"),sQuery(id+"F0.wireOp",EDGE,"E11.6.2.0"),sQuery(id+"F0.wireOp",EDGE,"E11.6.3.0"),sQuery(id+"F0.wireOp",EDGE,"E11.6.4.0"),sQuery(id+"F0.wireOp",EDGE,"E11.6.5.0"),sQuery(id+"F0.wireOp",EDGE,"E11.6.6.0"),sQuery(id+"F0.wireOp",EDGE,"E11.6.7.0"),sQuery(id+"F0.wireOp",EDGE,"E11.7.0.0"),sQuery(id+"F0.wireOp",EDGE,"E11.7.1.0"),sQuery(id+"F0.wireOp",EDGE,"E11.7.2.0"),sQuery(id+"F0.wireOp",EDGE,"E11.7.3.0"),sQuery(id+"F0.wireOp",EDGE,"E11.7.4.0"),sQuery(id+"F0.wireOp",EDGE,"E11.7.5.0"),sQuery(id+"F0.wireOp",EDGE,"E11.7.6.0"),sQuery(id+"F0.wireOp",EDGE,"E11.7.7.0"),sQuery(id+"F0.wireOp",EDGE,"E22"),sQuery(id+"F0.wireOp",EDGE,"E23"),sQuery(id+"F0.wireOp",EDGE,"E24"),sQuery(id+"F0.wireOp",EDGE,"E25"),sQuery(id+"F0.wireOp",EDGE,"E26"),sQuery(id+"F0.wireOp",EDGE,"E27"),sQuery(id+"F0.wireOp",EDGE,"E28"),sQuery(id+"F0.wireOp",EDGE,"E29"),sQuery(id+"F0.wireOp",EDGE,"E30")])],"isStart":false});
            var sketch = newSketch(context, id + "F4", { "sketchPlane" : qUnion([Q0])});
            skLineSegment(sketch, "E33", {"start": v(228.93, -12.7) * mm, "end": v(230.43, -54.97) * mm});
            skLineSegment(sketch, "E34", {"start": v(228.93, -12.7) * mm, "end": v(228.93, 548.23) * mm});
            skLineSegment(sketch, "E35", {"start": v(228.93, 548.23) * mm, "end": v(533.06, 548.23) * mm});
            skLineSegment(sketch, "E36", {"start": v(533.06, 548.23) * mm, "end": v(533.06, -54.97) * mm});
            skLineSegment(sketch, "E37", {"start": v(533.06, -54.97) * mm, "end": v(-92.7, -54.97) * mm});
            skLineSegment(sketch, "E38", {"start": v(-92.7, -54.97) * mm, "end": v(-92.7, 228.93) * mm});
            skPoint(sketch, "E38.endSnap0", {"position": v(469.9, 228.93) * mm});
            skLineSegment(sketch, "E39", {"start": v(-92.7, 228.93) * mm, "end": v(228.93, 228.93) * mm});
            skSolve(sketch);
        }
        {
            var Q0;
            {var subQ11=sQuery(id+"F4.wireOp",EDGE,"E33");Q0=makeQuery(id+"F4.imprint","IMPRINT",FACE,{"disambiguationData":[TD([[makeQuery(id+"F4.imprint","IMPRINT",EDGE,{"derivedFrom":subQ11}),1.0]])]});}
            var Q1;
            {var subQ11=sQuery(id+"F4.wireOp",EDGE,"E33");Q1=makeQuery(id+"F4.imprint","IMPRINT",FACE,{"disambiguationData":[TD([[makeQuery(id+"F4.imprint","IMPRINT",EDGE,{"derivedFrom":subQ11}),-1.0]])]});}
            var Q2;
            Q2=makeQuery(id+"F4.imprint","IMPRINT",FACE,{"disambiguationData":[TD([[makeQuery(id+"F4.imprint","IMPRINT",EDGE,{"derivedFrom":makeQuery(id+"F1.opExtrude","CAP_EDGE",EDGE,{"disambiguationData":[OSD([sQuery(id+"F0.wireOp",EDGE,"E11.1.6.0")])],"isStart":false})}),1.0]])]});
            var Q3;
            {var subQ20=sQuery(id+"F0.wireOp",EDGE,"E11.0.4.0");Q3=makeQuery(id+"F4.imprint","IMPRINT",FACE,{"disambiguationData":[TD([[makeQuery(id+"F4.imprint","IMPRINT",EDGE,{"derivedFrom":makeQuery(id+"F1.opExtrude","CAP_EDGE",EDGE,{"disambiguationData":[OSD([subQ20])],"isStart":false})}),-1.0]])]});}
            var Q4;
            {var subQ13=sQuery(id+"F0.wireOp",EDGE,"E11.4.0.0");Q4=makeQuery(id+"F4.imprint","IMPRINT",FACE,{"disambiguationData":[TD([[makeQuery(id+"F4.imprint","IMPRINT",EDGE,{"derivedFrom":makeQuery(id+"F1.opExtrude","CAP_EDGE",EDGE,{"disambiguationData":[OSD([subQ13])],"isStart":false})}),-1.0]])]});}
            var Q5;
            Q5=makeQuery(id+"F4.imprint","IMPRINT",FACE,{"disambiguationData":[TD([[makeQuery(id+"F4.imprint","IMPRINT",EDGE,{"derivedFrom":makeQuery(id+"F1.opExtrude","CAP_EDGE",EDGE,{"disambiguationData":[OSD([sQuery(id+"F0.wireOp",EDGE,"E11.0.4.0")])],"isStart":false})}),1.0]])]});
            var Q6;
            Q6=makeQuery(id+"F4.imprint","IMPRINT",FACE,{"disambiguationData":[TD([[makeQuery(id+"F4.imprint","IMPRINT",EDGE,{"derivedFrom":makeQuery(id+"F1.opExtrude","CAP_EDGE",EDGE,{"disambiguationData":[OSD([sQuery(id+"F0.wireOp",EDGE,"E11.0.5.0")])],"isStart":false})}),1.0]])]});
            var Q7;
            Q7=makeQuery(id+"F4.imprint","IMPRINT",FACE,{"disambiguationData":[TD([[makeQuery(id+"F4.imprint","IMPRINT",EDGE,{"derivedFrom":makeQuery(id+"F1.opExtrude","CAP_EDGE",EDGE,{"disambiguationData":[OSD([sQuery(id+"F0.wireOp",EDGE,"E11.1.5.0")])],"isStart":false})}),1.0]])]});
            var Q8;
            Q8=makeQuery(id+"F4.imprint","IMPRINT",FACE,{"disambiguationData":[TD([[makeQuery(id+"F4.imprint","IMPRINT",EDGE,{"derivedFrom":makeQuery(id+"F1.opExtrude","CAP_EDGE",EDGE,{"disambiguationData":[OSD([sQuery(id+"F0.wireOp",EDGE,"E11.1.4.0")])],"isStart":false})}),1.0]])]});
            var Q9;
            Q9=makeQuery(id+"F4.imprint","IMPRINT",FACE,{"disambiguationData":[TD([[makeQuery(id+"F4.imprint","IMPRINT",EDGE,{"derivedFrom":makeQuery(id+"F1.opExtrude","CAP_EDGE",EDGE,{"disambiguationData":[OSD([sQuery(id+"F0.wireOp",EDGE,"E11.2.4.0")])],"isStart":false})}),1.0]])]});
            var Q10;
            Q10=makeQuery(id+"F4.imprint","IMPRINT",FACE,{"disambiguationData":[TD([[makeQuery(id+"F4.imprint","IMPRINT",EDGE,{"derivedFrom":makeQuery(id+"F1.opExtrude","CAP_EDGE",EDGE,{"disambiguationData":[OSD([sQuery(id+"F0.wireOp",EDGE,"E11.2.5.0")])],"isStart":false})}),1.0]])]});
            var Q11;
            Q11=makeQuery(id+"F4.imprint","IMPRINT",FACE,{"disambiguationData":[TD([[makeQuery(id+"F4.imprint","IMPRINT",EDGE,{"derivedFrom":makeQuery(id+"F1.opExtrude","CAP_EDGE",EDGE,{"disambiguationData":[OSD([sQuery(id+"F0.wireOp",EDGE,"E11.3.5.0")])],"isStart":false})}),1.0]])]});
            var Q12;
            Q12=makeQuery(id+"F4.imprint","IMPRINT",FACE,{"disambiguationData":[TD([[makeQuery(id+"F4.imprint","IMPRINT",EDGE,{"derivedFrom":makeQuery(id+"F1.opExtrude","CAP_EDGE",EDGE,{"disambiguationData":[OSD([sQuery(id+"F0.wireOp",EDGE,"E11.3.4.0")])],"isStart":false})}),1.0]])]});
            var Q13;
            Q13=makeQuery(id+"F4.imprint","IMPRINT",FACE,{"disambiguationData":[TD([[makeQuery(id+"F4.imprint","IMPRINT",EDGE,{"derivedFrom":makeQuery(id+"F1.opExtrude","CAP_EDGE",EDGE,{"disambiguationData":[OSD([sQuery(id+"F0.wireOp",EDGE,"E11.4.5.0")])],"isStart":false})}),1.0]])]});
            var Q14;
            Q14=makeQuery(id+"F4.imprint","IMPRINT",FACE,{"disambiguationData":[TD([[makeQuery(id+"F4.imprint","IMPRINT",EDGE,{"derivedFrom":makeQuery(id+"F1.opExtrude","CAP_EDGE",EDGE,{"disambiguationData":[OSD([sQuery(id+"F0.wireOp",EDGE,"E11.4.4.0")])],"isStart":false})}),1.0]])]});
            var Q15;
            Q15=makeQuery(id+"F4.imprint","IMPRINT",FACE,{"disambiguationData":[TD([[makeQuery(id+"F4.imprint","IMPRINT",EDGE,{"derivedFrom":makeQuery(id+"F1.opExtrude","CAP_EDGE",EDGE,{"disambiguationData":[OSD([sQuery(id+"F0.wireOp",EDGE,"E11.5.4.0")])],"isStart":false})}),1.0]])]});
            var Q16;
            Q16=makeQuery(id+"F4.imprint","IMPRINT",FACE,{"disambiguationData":[TD([[makeQuery(id+"F4.imprint","IMPRINT",EDGE,{"derivedFrom":makeQuery(id+"F1.opExtrude","CAP_EDGE",EDGE,{"disambiguationData":[OSD([sQuery(id+"F0.wireOp",EDGE,"E11.5.5.0")])],"isStart":false})}),1.0]])]});
            var Q17;
            Q17=makeQuery(id+"F4.imprint","IMPRINT",FACE,{"disambiguationData":[TD([[makeQuery(id+"F4.imprint","IMPRINT",EDGE,{"derivedFrom":makeQuery(id+"F1.opExtrude","CAP_EDGE",EDGE,{"disambiguationData":[OSD([sQuery(id+"F0.wireOp",EDGE,"E11.6.5.0")])],"isStart":false})}),1.0]])]});
            var Q18;
            Q18=makeQuery(id+"F4.imprint","IMPRINT",FACE,{"disambiguationData":[TD([[makeQuery(id+"F4.imprint","IMPRINT",EDGE,{"derivedFrom":makeQuery(id+"F1.opExtrude","CAP_EDGE",EDGE,{"disambiguationData":[OSD([sQuery(id+"F0.wireOp",EDGE,"E11.6.4.0")])],"isStart":false})}),1.0]])]});
            var Q19;
            Q19=makeQuery(id+"F4.imprint","IMPRINT",FACE,{"disambiguationData":[TD([[makeQuery(id+"F4.imprint","IMPRINT",EDGE,{"derivedFrom":makeQuery(id+"F1.opExtrude","CAP_EDGE",EDGE,{"disambiguationData":[OSD([sQuery(id+"F0.wireOp",EDGE,"E11.7.4.0")])],"isStart":false})}),1.0]])]});
            var Q20;
            Q20=makeQuery(id+"F4.imprint","IMPRINT",FACE,{"disambiguationData":[TD([[makeQuery(id+"F4.imprint","IMPRINT",EDGE,{"derivedFrom":makeQuery(id+"F1.opExtrude","CAP_EDGE",EDGE,{"disambiguationData":[OSD([sQuery(id+"F0.wireOp",EDGE,"E11.7.5.0")])],"isStart":false})}),1.0]])]});
            var Q21;
            Q21=makeQuery(id+"F4.imprint","IMPRINT",FACE,{"disambiguationData":[TD([[makeQuery(id+"F4.imprint","IMPRINT",EDGE,{"derivedFrom":makeQuery(id+"F1.opExtrude","CAP_EDGE",EDGE,{"disambiguationData":[OSD([sQuery(id+"F0.wireOp",EDGE,"E11.7.6.0")])],"isStart":false})}),1.0]])]});
            var Q22;
            Q22=makeQuery(id+"F4.imprint","IMPRINT",FACE,{"disambiguationData":[TD([[makeQuery(id+"F4.imprint","IMPRINT",EDGE,{"derivedFrom":makeQuery(id+"F1.opExtrude","CAP_EDGE",EDGE,{"disambiguationData":[OSD([sQuery(id+"F0.wireOp",EDGE,"E11.6.6.0")])],"isStart":false})}),1.0]])]});
            var Q23;
            Q23=makeQuery(id+"F4.imprint","IMPRINT",FACE,{"disambiguationData":[TD([[makeQuery(id+"F4.imprint","IMPRINT",EDGE,{"derivedFrom":makeQuery(id+"F1.opExtrude","CAP_EDGE",EDGE,{"disambiguationData":[OSD([sQuery(id+"F0.wireOp",EDGE,"E11.5.6.0")])],"isStart":false})}),1.0]])]});
            var Q24;
            Q24=makeQuery(id+"F4.imprint","IMPRINT",FACE,{"disambiguationData":[TD([[makeQuery(id+"F4.imprint","IMPRINT",EDGE,{"derivedFrom":makeQuery(id+"F1.opExtrude","CAP_EDGE",EDGE,{"disambiguationData":[OSD([sQuery(id+"F0.wireOp",EDGE,"E11.4.6.0")])],"isStart":false})}),1.0]])]});
            var Q25;
            Q25=makeQuery(id+"F4.imprint","IMPRINT",FACE,{"disambiguationData":[TD([[makeQuery(id+"F4.imprint","IMPRINT",EDGE,{"derivedFrom":makeQuery(id+"F1.opExtrude","CAP_EDGE",EDGE,{"disambiguationData":[OSD([sQuery(id+"F0.wireOp",EDGE,"E11.3.6.0")])],"isStart":false})}),1.0]])]});
            var Q26;
            Q26=makeQuery(id+"F4.imprint","IMPRINT",FACE,{"disambiguationData":[TD([[makeQuery(id+"F4.imprint","IMPRINT",EDGE,{"derivedFrom":makeQuery(id+"F1.opExtrude","CAP_EDGE",EDGE,{"disambiguationData":[OSD([sQuery(id+"F0.wireOp",EDGE,"E11.2.6.0")])],"isStart":false})}),1.0]])]});
            var Q27;
            Q27=makeQuery(id+"F4.imprint","IMPRINT",FACE,{"disambiguationData":[TD([[makeQuery(id+"F4.imprint","IMPRINT",EDGE,{"derivedFrom":makeQuery(id+"F1.opExtrude","CAP_EDGE",EDGE,{"disambiguationData":[OSD([sQuery(id+"F0.wireOp",EDGE,"E11.2.7.0")])],"isStart":false})}),1.0]])]});
            var Q28;
            Q28=makeQuery(id+"F4.imprint","IMPRINT",FACE,{"disambiguationData":[TD([[makeQuery(id+"F4.imprint","IMPRINT",EDGE,{"derivedFrom":makeQuery(id+"F1.opExtrude","CAP_EDGE",EDGE,{"disambiguationData":[OSD([sQuery(id+"F0.wireOp",EDGE,"E11.1.7.0")])],"isStart":false})}),1.0]])]});
            var Q29;
            Q29=makeQuery(id+"F4.imprint","IMPRINT",FACE,{"disambiguationData":[TD([[makeQuery(id+"F4.imprint","IMPRINT",EDGE,{"derivedFrom":makeQuery(id+"F1.opExtrude","CAP_EDGE",EDGE,{"disambiguationData":[OSD([sQuery(id+"F0.wireOp",EDGE,"E11.0.7.0")])],"isStart":false})}),1.0]])]});
            var Q30;
            Q30=makeQuery(id+"F4.imprint","IMPRINT",FACE,{"disambiguationData":[TD([[makeQuery(id+"F4.imprint","IMPRINT",EDGE,{"derivedFrom":makeQuery(id+"F1.opExtrude","CAP_EDGE",EDGE,{"disambiguationData":[OSD([sQuery(id+"F0.wireOp",EDGE,"E11.0.6.0")])],"isStart":false})}),1.0]])]});
            var Q31;
            Q31=makeQuery(id+"F4.imprint","IMPRINT",FACE,{"disambiguationData":[TD([[makeQuery(id+"F4.imprint","IMPRINT",EDGE,{"derivedFrom":makeQuery(id+"F1.opExtrude","CAP_EDGE",EDGE,{"disambiguationData":[OSD([sQuery(id+"F0.wireOp",EDGE,"E11.4.7.0")])],"isStart":false})}),1.0]])]});
            var Q32;
            Q32=makeQuery(id+"F4.imprint","IMPRINT",FACE,{"disambiguationData":[TD([[makeQuery(id+"F4.imprint","IMPRINT",EDGE,{"derivedFrom":makeQuery(id+"F1.opExtrude","CAP_EDGE",EDGE,{"disambiguationData":[OSD([sQuery(id+"F0.wireOp",EDGE,"E11.5.7.0")])],"isStart":false})}),1.0]])]});
            var Q33;
            Q33=makeQuery(id+"F4.imprint","IMPRINT",FACE,{"disambiguationData":[TD([[makeQuery(id+"F4.imprint","IMPRINT",EDGE,{"derivedFrom":makeQuery(id+"F1.opExtrude","CAP_EDGE",EDGE,{"disambiguationData":[OSD([sQuery(id+"F0.wireOp",EDGE,"E11.6.7.0")])],"isStart":false})}),1.0]])]});
            var Q34;
            Q34=makeQuery(id+"F4.imprint","IMPRINT",FACE,{"disambiguationData":[TD([[makeQuery(id+"F4.imprint","IMPRINT",EDGE,{"derivedFrom":makeQuery(id+"F1.opExtrude","CAP_EDGE",EDGE,{"disambiguationData":[OSD([sQuery(id+"F0.wireOp",EDGE,"E11.7.7.0")])],"isStart":false})}),1.0]])]});
            var Q35;
            Q35=makeQuery(id+"F4.imprint","IMPRINT",FACE,{"disambiguationData":[TD([[makeQuery(id+"F4.imprint","IMPRINT",EDGE,{"derivedFrom":makeQuery(id+"F1.opExtrude","CAP_EDGE",EDGE,{"disambiguationData":[OSD([sQuery(id+"F0.wireOp",EDGE,"E11.4.0.0")])],"isStart":false})}),1.0]])]});
            var Q36;
            Q36=makeQuery(id+"F4.imprint","IMPRINT",FACE,{"disambiguationData":[TD([[makeQuery(id+"F4.imprint","IMPRINT",EDGE,{"derivedFrom":makeQuery(id+"F1.opExtrude","CAP_EDGE",EDGE,{"disambiguationData":[OSD([sQuery(id+"F0.wireOp",EDGE,"E11.5.0.0")])],"isStart":false})}),1.0]])]});
            var Q37;
            Q37=makeQuery(id+"F4.imprint","IMPRINT",FACE,{"disambiguationData":[TD([[makeQuery(id+"F4.imprint","IMPRINT",EDGE,{"derivedFrom":makeQuery(id+"F1.opExtrude","CAP_EDGE",EDGE,{"disambiguationData":[OSD([sQuery(id+"F0.wireOp",EDGE,"E11.6.0.0")])],"isStart":false})}),1.0]])]});
            var Q38;
            Q38=makeQuery(id+"F4.imprint","IMPRINT",FACE,{"disambiguationData":[TD([[makeQuery(id+"F4.imprint","IMPRINT",EDGE,{"derivedFrom":makeQuery(id+"F1.opExtrude","CAP_EDGE",EDGE,{"disambiguationData":[OSD([sQuery(id+"F0.wireOp",EDGE,"E11.7.0.0")])],"isStart":false})}),1.0]])]});
            var Q39;
            Q39=makeQuery(id+"F4.imprint","IMPRINT",FACE,{"disambiguationData":[TD([[makeQuery(id+"F4.imprint","IMPRINT",EDGE,{"derivedFrom":makeQuery(id+"F1.opExtrude","CAP_EDGE",EDGE,{"disambiguationData":[OSD([sQuery(id+"F0.wireOp",EDGE,"E11.3.7.0")])],"isStart":false})}),1.0]])]});
            var Q40;
            Q40=makeQuery(id+"F4.imprint","IMPRINT",FACE,{"disambiguationData":[TD([[makeQuery(id+"F4.imprint","IMPRINT",EDGE,{"derivedFrom":makeQuery(id+"F1.opExtrude","CAP_EDGE",EDGE,{"disambiguationData":[OSD([sQuery(id+"F0.wireOp",EDGE,"E11.7.3.0")])],"isStart":false})}),1.0]])]});
            var Q41;
            Q41=makeQuery(id+"F4.imprint","IMPRINT",FACE,{"disambiguationData":[TD([[makeQuery(id+"F4.imprint","IMPRINT",EDGE,{"derivedFrom":makeQuery(id+"F1.opExtrude","CAP_EDGE",EDGE,{"disambiguationData":[OSD([sQuery(id+"F0.wireOp",EDGE,"E11.7.2.0")])],"isStart":false})}),1.0]])]});
            var Q42;
            Q42=makeQuery(id+"F4.imprint","IMPRINT",FACE,{"disambiguationData":[TD([[makeQuery(id+"F4.imprint","IMPRINT",EDGE,{"derivedFrom":makeQuery(id+"F1.opExtrude","CAP_EDGE",EDGE,{"disambiguationData":[OSD([sQuery(id+"F0.wireOp",EDGE,"E11.6.2.0")])],"isStart":false})}),1.0]])]});
            var Q43;
            Q43=makeQuery(id+"F4.imprint","IMPRINT",FACE,{"disambiguationData":[TD([[makeQuery(id+"F4.imprint","IMPRINT",EDGE,{"derivedFrom":makeQuery(id+"F1.opExtrude","CAP_EDGE",EDGE,{"disambiguationData":[OSD([sQuery(id+"F0.wireOp",EDGE,"E11.6.1.0")])],"isStart":false})}),1.0]])]});
            var Q44;
            Q44=makeQuery(id+"F4.imprint","IMPRINT",FACE,{"disambiguationData":[TD([[makeQuery(id+"F4.imprint","IMPRINT",EDGE,{"derivedFrom":makeQuery(id+"F1.opExtrude","CAP_EDGE",EDGE,{"disambiguationData":[OSD([sQuery(id+"F0.wireOp",EDGE,"E11.7.1.0")])],"isStart":false})}),1.0]])]});
            var Q45;
            Q45=makeQuery(id+"F4.imprint","IMPRINT",FACE,{"disambiguationData":[TD([[makeQuery(id+"F4.imprint","IMPRINT",EDGE,{"derivedFrom":makeQuery(id+"F1.opExtrude","CAP_EDGE",EDGE,{"disambiguationData":[OSD([sQuery(id+"F0.wireOp",EDGE,"E11.6.3.0")])],"isStart":false})}),1.0]])]});
            var Q46;
            Q46=makeQuery(id+"F4.imprint","IMPRINT",FACE,{"disambiguationData":[TD([[makeQuery(id+"F4.imprint","IMPRINT",EDGE,{"derivedFrom":makeQuery(id+"F1.opExtrude","CAP_EDGE",EDGE,{"disambiguationData":[OSD([sQuery(id+"F0.wireOp",EDGE,"E11.5.3.0")])],"isStart":false})}),1.0]])]});
            var Q47;
            Q47=makeQuery(id+"F4.imprint","IMPRINT",FACE,{"disambiguationData":[TD([[makeQuery(id+"F4.imprint","IMPRINT",EDGE,{"derivedFrom":makeQuery(id+"F1.opExtrude","CAP_EDGE",EDGE,{"disambiguationData":[OSD([sQuery(id+"F0.wireOp",EDGE,"E11.5.2.0")])],"isStart":false})}),1.0]])]});
            var Q48;
            Q48=makeQuery(id+"F4.imprint","IMPRINT",FACE,{"disambiguationData":[TD([[makeQuery(id+"F4.imprint","IMPRINT",EDGE,{"derivedFrom":makeQuery(id+"F1.opExtrude","CAP_EDGE",EDGE,{"disambiguationData":[OSD([sQuery(id+"F0.wireOp",EDGE,"E11.5.1.0")])],"isStart":false})}),1.0]])]});
            var Q49;
            Q49=makeQuery(id+"F4.imprint","IMPRINT",FACE,{"disambiguationData":[TD([[makeQuery(id+"F4.imprint","IMPRINT",EDGE,{"derivedFrom":makeQuery(id+"F1.opExtrude","CAP_EDGE",EDGE,{"disambiguationData":[OSD([sQuery(id+"F0.wireOp",EDGE,"E11.4.1.0")])],"isStart":false})}),1.0]])]});
            var Q50;
            Q50=makeQuery(id+"F4.imprint","IMPRINT",FACE,{"disambiguationData":[TD([[makeQuery(id+"F4.imprint","IMPRINT",EDGE,{"derivedFrom":makeQuery(id+"F1.opExtrude","CAP_EDGE",EDGE,{"disambiguationData":[OSD([sQuery(id+"F0.wireOp",EDGE,"E11.4.2.0")])],"isStart":false})}),1.0]])]});
            var Q51;
            Q51=makeQuery(id+"F4.imprint","IMPRINT",FACE,{"disambiguationData":[TD([[makeQuery(id+"F4.imprint","IMPRINT",EDGE,{"derivedFrom":makeQuery(id+"F1.opExtrude","CAP_EDGE",EDGE,{"disambiguationData":[OSD([sQuery(id+"F0.wireOp",EDGE,"E11.4.3.0")])],"isStart":false})}),1.0]])]});
            extrude(context, id + "F5", {"entities" : qUnion([Q0, Q1, Q2, Q3, Q4, Q5, Q6, Q7, Q8, Q9, Q10, Q11, Q12, Q13, Q14, Q15, Q16, Q17, Q18, Q19, Q20, Q21, Q22, Q23, Q24, Q25, Q26, Q27, Q28, Q29, Q30, Q31, Q32, Q33, Q34, Q35, Q36, Q37, Q38, Q39, Q40, Q41, Q42, Q43, Q44, Q45, Q46, Q47, Q48, Q49, Q50, Q51]), "operationType" : NewBodyOperationType.REMOVE, "oppositeDirection" : true, "depth" : 101.6 * mm, "offsetDistance" : 25.4 * mm, "symmetric" : true});
        }
        {
            var Q0;
            Q0=qCreatedBy(makeId("Front.planeOp"),FACE);
            var sketch = newSketch(context, id + "F6", { "sketchPlane" : qUnion([Q0])});
            skLineSegment(sketch, "E40", {"start": v(0, 228.28) * mm, "end": v(0.33, 342.9) * mm, "construction": true});
            skLineSegment(sketch, "E41", {"start": v(0.33, 342.9) * mm, "end": v(228.93, 342.9) * mm, "construction": true});
            skLineSegment(sketch, "E42", {"start": v(228.93, 342.9) * mm, "end": v(236.55, 342.9) * mm, "construction": true});
            skLineSegment(sketch, "E43", {"start": v(236.55, 351.7) * mm, "end": v(232.74, 351.7) * mm, "construction": true});
            skLineSegment(sketch, "E44", {"start": v(234.64, 351.7) * mm, "end": v(234.64, 352.98) * mm, "construction": true});
            skArc(sketch, "E45", {"start": v(236.55, 351.7) * mm, "mid": v(234.64, 352.99) * mm, "end": v(232.74, 351.7) * mm});
            skLineSegment(sketch, "E46", {"start": v(232.74, 349.69) * mm, "end": v(228.93, 349.69) * mm});
            skLineSegment(sketch, "E47", {"start": v(232.74, 349.69) * mm, "end": v(232.74, 351.7) * mm});
            skLineSegment(sketch, "E48", {"start": v(236.55, 351.7) * mm, "end": v(236.55, 342.9) * mm});
            skLineSegment(sketch, "E49.MirrorCS", {"start": v(232.74, 336.12) * mm, "end": v(228.93, 336.12) * mm});
            skLineSegment(sketch, "E50.MirrorCS", {"start": v(236.55, 334.1) * mm, "end": v(232.74, 334.1) * mm, "construction": true});
            skArc(sketch, "E51.MirrorCS", {"start": v(236.55, 334.1) * mm, "mid": v(234.64, 332.82) * mm, "end": v(232.74, 334.1) * mm});
            skLineSegment(sketch, "E52", {"start": v(232.74, 336.12) * mm, "end": v(232.74, 334.1) * mm});
            skLineSegment(sketch, "E53", {"start": v(236.55, 334.1) * mm, "end": v(236.55, 342.9) * mm});
            skLineSegment(sketch, "E54", {"start": v(228.93, 349.69) * mm, "end": v(228.93, 336.12) * mm});
            skLineSegment(sketch, "E55", {"start": v(114.63, 342.9) * mm, "end": v(114.63, 228.93) * mm, "construction": true});
            skLineSegment(sketch, "E56.direction2", {"start": v(228.93, 349.69) * mm, "end": v(228.93, 406.84) * mm, "construction": true});
            skArc(sketch, "E57.0.1.0", {"start": v(236.55, 293.5) * mm, "mid": v(234.64, 294.79) * mm, "end": v(232.74, 293.5) * mm});
            skLineSegment(sketch, "E57.0.1.1", {"start": v(232.74, 291.49) * mm, "end": v(232.74, 293.5) * mm});
            skLineSegment(sketch, "E57.0.1.2", {"start": v(232.74, 291.49) * mm, "end": v(228.93, 291.49) * mm});
            skLineSegment(sketch, "E57.0.1.3", {"start": v(236.55, 293.5) * mm, "end": v(236.55, 285.51) * mm});
            skLineSegment(sketch, "E57.0.1.4", {"start": v(236.55, 277.52) * mm, "end": v(236.55, 285.51) * mm});
            skArc(sketch, "E57.0.1.5", {"start": v(236.55, 277.52) * mm, "mid": v(234.64, 276.24) * mm, "end": v(232.74, 277.52) * mm});
            skLineSegment(sketch, "E57.0.1.6", {"start": v(232.74, 279.54) * mm, "end": v(232.74, 277.52) * mm});
            skLineSegment(sketch, "E57.0.1.7", {"start": v(232.74, 279.54) * mm, "end": v(228.93, 279.54) * mm});
            skLineSegment(sketch, "E58", {"start": v(228.93, 291.49) * mm, "end": v(228.93, 279.54) * mm});
            skLineSegment(sketch, "E59.MirrorCS", {"start": v(128.06, 342.87) * mm, "end": v(127.33, 228.9) * mm, "construction": true});
            skLineSegment(sketch, "E60", {"start": v(142.97, 228.93) * mm, "end": v(142.97, 238.08) * mm, "construction": true});
            skPoint(sketch, "E60.endSnap0", {"position": v(142.97, 228.93) * mm});
            skLineSegment(sketch, "E61.MirrorCS", {"start": v(164.9, 228.93) * mm, "end": v(164.9, 232.87) * mm});
            skLineSegment(sketch, "E62.MirrorCS", {"start": v(165.06, 232.86) * mm, "end": v(163.66, 232.85) * mm});
            skArc(sketch, "E63.MirrorCS", {"start": v(163.66, 232.85) * mm, "mid": v(162.47, 234.78) * mm, "end": v(163.66, 236.71) * mm});
            skLineSegment(sketch, "E64.MirrorCS", {"start": v(163.66, 236.71) * mm, "end": v(171.53, 236.73) * mm});
            skLineSegment(sketch, "E65.MirrorCS", {"start": v(179.4, 236.62) * mm, "end": v(171.53, 236.6) * mm});
            skLineSegment(sketch, "E66.MirrorCS", {"start": v(178.01, 232.76) * mm, "end": v(179.4, 232.76) * mm});
            skArc(sketch, "E67.MirrorCS", {"start": v(179.4, 232.76) * mm, "mid": v(180.6, 234.7) * mm, "end": v(179.4, 236.62) * mm});
            skLineSegment(sketch, "E68.MirrorCS", {"start": v(178.02, 228.95) * mm, "end": v(171.54, 228.93) * mm});
            skLineSegment(sketch, "E69", {"start": v(171.38, 228.95) * mm, "end": v(164.9, 228.93) * mm, "construction": true});
            skLineSegment(sketch, "E70", {"start": v(178.02, 228.95) * mm, "end": v(178.01, 232.76) * mm});
            skLineSegment(sketch, "E71", {"start": v(171.38, 228.95) * mm, "end": v(164.9, 228.93) * mm});
            skLineSegment(sketch, "E72", {"start": v(85.82, 228.93) * mm, "end": v(85.82, 235.35) * mm, "construction": true});
            skLineSegment(sketch, "E73", {"start": v(57.24, 228.93) * mm, "end": v(58.79, 224.1) * mm, "construction": true});
            skLineSegment(sketch, "E74.1.0.0", {"start": v(179.42, 236.59) * mm, "end": v(171.56, 236.6) * mm});
            skLineSegment(sketch, "E74.1.0.1", {"start": v(163.7, 236.62) * mm, "end": v(171.56, 236.6) * mm});
            skArc(sketch, "E74.1.0.2", {"start": v(163.68, 232.76) * mm, "mid": v(162.5, 234.7) * mm, "end": v(163.7, 236.62) * mm});
            skLineSegment(sketch, "E74.1.0.3", {"start": v(165.07, 232.76) * mm, "end": v(163.68, 232.76) * mm});
            skLineSegment(sketch, "E74.1.0.4", {"start": v(165.06, 228.95) * mm, "end": v(165.07, 232.76) * mm});
            skArc(sketch, "E74.1.0.5", {"start": v(179.42, 232.73) * mm, "mid": v(180.62, 234.66) * mm, "end": v(179.42, 236.59) * mm});
            skLineSegment(sketch, "E74.1.0.6", {"start": v(178.03, 232.73) * mm, "end": v(179.42, 232.73) * mm});
            skLineSegment(sketch, "E74.1.0.7", {"start": v(178.02, 228.92) * mm, "end": v(178.03, 232.73) * mm});
            skLineSegment(sketch, "E74.1.0.8", {"start": v(178.02, 228.92) * mm, "end": v(171.54, 228.93) * mm});
            skLineSegment(sketch, "E74.1.0.9", {"start": v(165.06, 228.95) * mm, "end": v(171.54, 228.93) * mm});
            skLineSegment(sketch, "E75.1.0.0", {"start": v(65.12, 236.71) * mm, "end": v(57.26, 236.73) * mm});
            skArc(sketch, "E75.1.0.1", {"start": v(65.12, 232.85) * mm, "mid": v(66.32, 234.78) * mm, "end": v(65.12, 236.71) * mm});
            skLineSegment(sketch, "E75.1.0.2", {"start": v(63.73, 232.86) * mm, "end": v(65.12, 232.85) * mm});
            skLineSegment(sketch, "E75.1.0.3", {"start": v(63.72, 228.92) * mm, "end": v(63.73, 232.86) * mm});
            skLineSegment(sketch, "E75.1.0.4", {"start": v(63.72, 228.92) * mm, "end": v(57.24, 228.93) * mm});
            skLineSegment(sketch, "E75.1.0.5", {"start": v(49.4, 236.75) * mm, "end": v(57.26, 236.73) * mm});
            skArc(sketch, "E75.1.0.6", {"start": v(49.38, 232.89) * mm, "mid": v(48.2, 234.82) * mm, "end": v(49.4, 236.75) * mm});
            skLineSegment(sketch, "E75.1.0.7", {"start": v(50.77, 232.88) * mm, "end": v(49.38, 232.89) * mm});
            skLineSegment(sketch, "E75.1.0.8", {"start": v(50.76, 228.95) * mm, "end": v(50.77, 232.88) * mm});
            skLineSegment(sketch, "E75.1.0.9", {"start": v(50.76, 228.95) * mm, "end": v(57.24, 228.93) * mm});
            skLineSegment(sketch, "E76", {"start": v(50.76, 228.95) * mm, "end": v(63.72, 228.92) * mm});
            skLineSegment(sketch, "E77", {"start": v(123.11, 232.78) * mm, "end": v(123.14, 236.64) * mm, "construction": true});
            skLineSegment(sketch, "E78", {"start": v(123.13, 234.7) * mm, "end": v(124.45, 234.7) * mm, "construction": true});
            skArc(sketch, "E79", {"start": v(123.11, 232.78) * mm, "mid": v(124.45, 234.7) * mm, "end": v(123.14, 236.64) * mm});
            skArc(sketch, "E80.MirrorCS", {"start": v(106.15, 232.78) * mm, "mid": v(104.81, 234.7) * mm, "end": v(106.12, 236.64) * mm});
            skLineSegment(sketch, "E81.MirrorCS", {"start": v(108.23, 232.8) * mm, "end": v(106.15, 232.78) * mm});
            skLineSegment(sketch, "E82.MirrorCS", {"start": v(108.23, 228.93) * mm, "end": v(108.23, 232.8) * mm});
            skLineSegment(sketch, "E83", {"start": v(106.12, 236.64) * mm, "end": v(123.14, 236.64) * mm});
            skLineSegment(sketch, "E84.0.1.0", {"start": v(232.74, 406.84) * mm, "end": v(228.93, 406.84) * mm});
            skLineSegment(sketch, "E84.0.1.1", {"start": v(232.74, 406.84) * mm, "end": v(232.74, 408.86) * mm});
            skArc(sketch, "E84.0.1.2", {"start": v(236.55, 408.86) * mm, "mid": v(234.64, 410.14) * mm, "end": v(232.74, 408.86) * mm});
            skLineSegment(sketch, "E84.0.1.3", {"start": v(236.55, 408.86) * mm, "end": v(236.55, 400.05) * mm});
            skLineSegment(sketch, "E84.0.1.4", {"start": v(236.55, 391.25) * mm, "end": v(236.55, 400.05) * mm});
            skArc(sketch, "E84.0.1.5", {"start": v(236.55, 391.25) * mm, "mid": v(234.64, 389.97) * mm, "end": v(232.74, 391.25) * mm});
            skLineSegment(sketch, "E84.0.1.6", {"start": v(232.74, 393.27) * mm, "end": v(232.74, 391.25) * mm});
            skLineSegment(sketch, "E84.0.1.7", {"start": v(232.74, 393.27) * mm, "end": v(228.93, 393.27) * mm});
            skLineSegment(sketch, "E84.0.1.8", {"start": v(228.93, 406.84) * mm, "end": v(228.93, 393.27) * mm});
            skLineSegment(sketch, "E84.direction1", {"start": v(228.93, 349.69) * mm, "end": v(254.33, 349.69) * mm, "construction": true});
            skLineSegment(sketch, "E85", {"start": v(108.23, 228.93) * mm, "end": v(121.03, 228.93) * mm});
            skLineSegment(sketch, "E86", {"start": v(114.63, 236.64) * mm, "end": v(114.63, 228.93) * mm});
            skLineSegment(sketch, "E87", {"start": v(121.03, 228.93) * mm, "end": v(121.03, 232.8) * mm});
            skLineSegment(sketch, "E88", {"start": v(121.03, 232.8) * mm, "end": v(123.11, 232.78) * mm});
            skSolve(sketch);
        }
        {
            var Q0;
            Q0=makeQuery(id+"F6.imprint","IMPRINT",FACE,{"disambiguationData":[TD([[makeQuery(id+"F6.imprint","IMPRINT",EDGE,{"derivedFrom":sQuery(id+"F6.wireOp",EDGE,"E57.0.1.0")}),1.0]])]});
            var Q1;
            Q1=makeQuery(id+"F6.imprint","IMPRINT",FACE,{"disambiguationData":[TD([[makeQuery(id+"F6.imprint","IMPRINT",EDGE,{"derivedFrom":sQuery(id+"F6.wireOp",EDGE,"E45")}),1.0]])]});
            var Q2;
            Q2=makeQuery(id+"F6.imprint","IMPRINT",FACE,{"disambiguationData":[TD([[makeQuery(id+"F6.imprint","IMPRINT",EDGE,{"derivedFrom":sQuery(id+"F6.wireOp",EDGE,"E84.0.1.0")}),1.0]])]});
            extrude(context, id + "F7", {"entities" : qUnion([Q0, Q1, Q2]), "operationType" : NewBodyOperationType.ADD, "depth" : 25.4 * mm, "offsetDistance" : 25.4 * mm});
        }
        {
            var Q0;
            Q0=qCreatedBy(makeId("Front.planeOp"),FACE);
            var sketch = newSketch(context, id + "F8", { "sketchPlane" : qUnion([Q0])});
            skLineSegment(sketch, "E89", {"start": v(123.12, 232.78) * mm, "end": v(123.14, 236.64) * mm, "construction": true});
            skLineSegment(sketch, "E90", {"start": v(123.13, 234.7) * mm, "end": v(124.45, 234.7) * mm, "construction": true});
            skArc(sketch, "E91", {"start": v(123.12, 232.78) * mm, "mid": v(124.45, 234.7) * mm, "end": v(123.14, 236.64) * mm});
            skArc(sketch, "E92.MirrorCS", {"start": v(106.14, 232.78) * mm, "mid": v(104.8, 234.7) * mm, "end": v(106.12, 236.64) * mm});
            skLineSegment(sketch, "E93.MirrorCS", {"start": v(108.23, 228.93) * mm, "end": v(108.23, 232.8) * mm});
            skLineSegment(sketch, "E94", {"start": v(108.23, 228.93) * mm, "end": v(121.04, 228.93) * mm});
            skLineSegment(sketch, "E95", {"start": v(121.04, 228.93) * mm, "end": v(121.04, 232.8) * mm});
            skLineSegment(sketch, "E96", {"start": v(121.04, 232.8) * mm, "end": v(123.12, 232.78) * mm});
            skLineSegment(sketch, "E97", {"start": v(106.12, 236.64) * mm, "end": v(123.14, 236.64) * mm});
            skLineSegment(sketch, "E98", {"start": v(106.14, 232.78) * mm, "end": v(108.23, 232.8) * mm});
            skLineSegment(sketch, "E99.1.0.0", {"start": v(163.27, 236.64) * mm, "end": v(180.3, 236.64) * mm});
            skArc(sketch, "E99.1.0.1", {"start": v(163.3, 232.78) * mm, "mid": v(161.96, 234.7) * mm, "end": v(163.27, 236.64) * mm});
            skLineSegment(sketch, "E99.1.0.2", {"start": v(163.3, 232.78) * mm, "end": v(165.38, 232.8) * mm});
            skLineSegment(sketch, "E99.1.0.3", {"start": v(165.38, 228.93) * mm, "end": v(165.38, 232.8) * mm});
            skLineSegment(sketch, "E99.1.0.4", {"start": v(165.38, 228.93) * mm, "end": v(178.19, 228.93) * mm});
            skLineSegment(sketch, "E99.1.0.5", {"start": v(178.19, 228.93) * mm, "end": v(178.19, 232.8) * mm});
            skLineSegment(sketch, "E99.1.0.6", {"start": v(178.19, 232.8) * mm, "end": v(180.27, 232.78) * mm});
            skArc(sketch, "E99.1.0.7", {"start": v(180.27, 232.78) * mm, "mid": v(181.6, 234.7) * mm, "end": v(180.3, 236.64) * mm});
            skLineSegment(sketch, "E100.1.0.0", {"start": v(48.97, 236.64) * mm, "end": v(66, 236.64) * mm});
            skLineSegment(sketch, "E100.1.0.1", {"start": v(49, 232.78) * mm, "end": v(51.08, 232.8) * mm});
            skLineSegment(sketch, "E100.1.0.2", {"start": v(51.08, 228.93) * mm, "end": v(51.08, 232.8) * mm});
            skArc(sketch, "E100.1.0.3", {"start": v(49, 232.78) * mm, "mid": v(47.66, 234.7) * mm, "end": v(48.97, 236.64) * mm});
            skLineSegment(sketch, "E100.1.0.4", {"start": v(63.89, 228.93) * mm, "end": v(63.89, 232.8) * mm});
            skLineSegment(sketch, "E100.1.0.5", {"start": v(63.89, 232.8) * mm, "end": v(65.97, 232.78) * mm});
            skArc(sketch, "E100.1.0.6", {"start": v(65.97, 232.78) * mm, "mid": v(67.3, 234.7) * mm, "end": v(66, 236.64) * mm});
            skLineSegment(sketch, "E101", {"start": v(51.08, 228.93) * mm, "end": v(63.89, 228.93) * mm});
            skSolve(sketch);
        }
        {
            var Q0;
            Q0=qSketchRegion(id+"F8",true);
            extrude(context, id + "F9", {"entities" : qUnion([Q0]), "operationType" : NewBodyOperationType.REMOVE, "endBound" : BoundingType.THROUGH_ALL, "depth" : 25.4 * mm, "offsetDistance" : 25.4 * mm});
        }
    });
